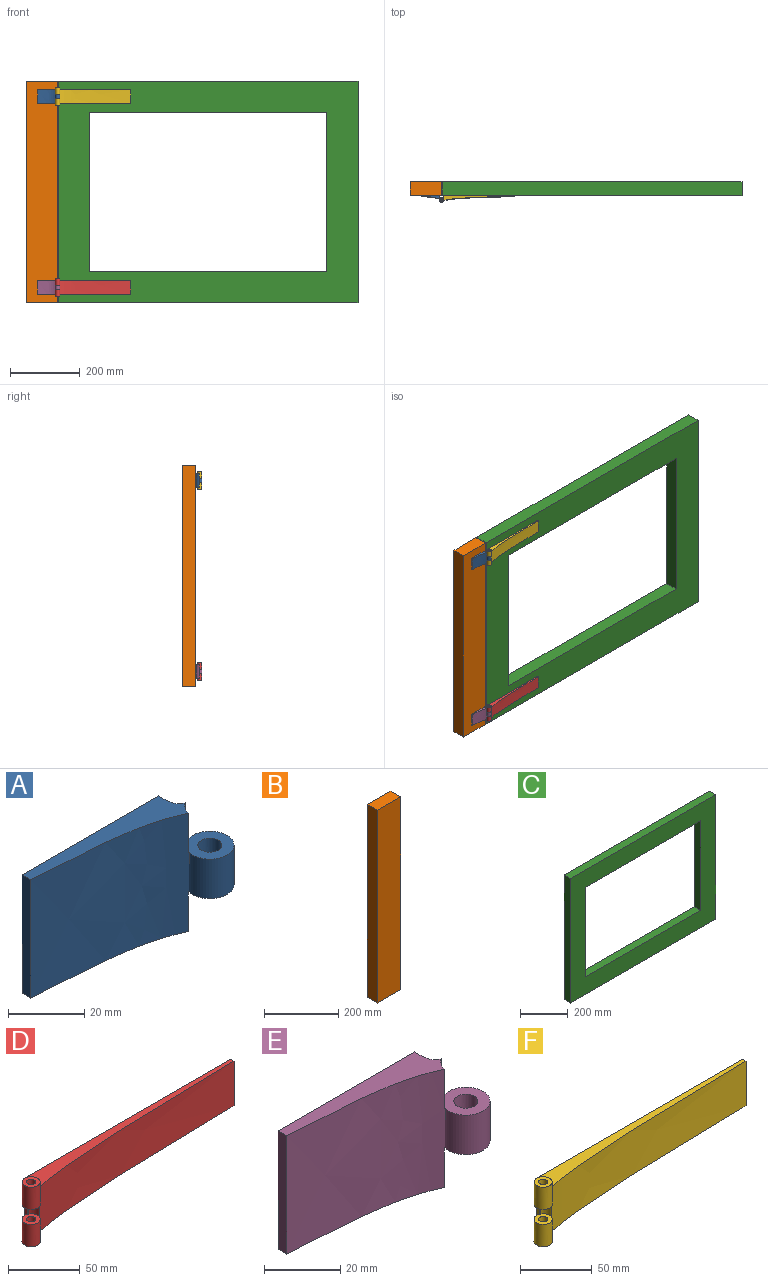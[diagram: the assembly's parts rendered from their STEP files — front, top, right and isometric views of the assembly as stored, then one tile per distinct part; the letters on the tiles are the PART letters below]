
ASSEMBLY  parts=6 mates=5
PART A: 13 faces, bbox 63.5x19.1x38.1 mm
  f0: cylinder r=6.35mm len=12.7mm, axis (0,0,1), area 443.4mm2, adj f1,f5,f8,f10
  f1: extruded ~38.1x4.05mm, area 204.5mm2, adj f0,f2,f6,f7,f8,f9,f10,f11
  f2: plane 38.1x3.18mm, normal (1,0,0), area 121mm2, adj f1,f3,f6,f7
  f3: plane 50.8x38.1mm, normal (0,1,0), area 1935.5mm2, adj f2,f4,f6,f7
  f4: plane 38.1x3.18mm, normal (-1,0,0), area 121mm2, adj f3,f5,f6,f7
  f5: extruded ~51x38.1mm, area 1971.3mm2, adj f0,f4,f6,f7,f8,f9,f10,f11
  f6: plane 53.65x11.1mm, normal (0,0,-1), area 293.4mm2, adj f1,f2,f3,f4,f5,f11
  f7: plane 53.65x11.1mm, normal (0,0,1), area 293.4mm2, adj f1,f2,f3,f4,f5,f9
  f8: plane 12.73x12.7mm, normal (0,0,1), area 96.3mm2, adj f0,f1,f5,f9,f12
  f9: cylinder r=6.6mm len=12.7mm, axis (0,0,1), area 62.1mm2, adj f1,f5,f7,f8
  f10: plane 12.73x12.7mm, normal (0,0,-1), area 96.3mm2, adj f0,f1,f5,f11,f12
  f11: cylinder r=6.6mm len=12.7mm, axis (0,0,-1), area 62.1mm2, adj f1,f5,f6,f10
  f12: cylinder r=3.17mm len=12.7mm, axis (0,0,1), area 253.4mm2, adj f8,f10
PART B: 6 faces, bbox 88.9x38.1x635 mm
  f0: plane 88.9x38.1mm, normal (0,0,1), area 3387.1mm2, adj f1,f3,f4,f5
  f1: plane 635x38.1mm, normal (-1,0,0), area 24193.5mm2, adj f0,f2,f4,f5
  f2: plane 88.9x38.1mm, normal (0,0,-1), area 3387.1mm2, adj f1,f3,f4,f5
  f3: plane 635x38.1mm, normal (1,0,0), area 24193.5mm2, adj f0,f2,f4,f5
  f4: plane 635x88.9mm, normal (0,-1,0), area 56451.5mm2, adj f0,f1,f2,f3
  f5: plane 635x88.9mm, normal (0,1,0), area 56451.5mm2, adj f0,f1,f2,f3
PART C: 10 faces, bbox 857.3x38.1x635 mm
  f0: plane 857.25x38.1mm, normal (0,0,1), area 32661.2mm2, adj f1,f7,f8,f9
  f1: plane 635x38.1mm, normal (-1,0,0), area 24193.5mm2, adj f0,f2,f8,f9
  f2: plane 857.25x38.1mm, normal (0,0,-1), area 32661.2mm2, adj f1,f7,f8,f9
  f3: plane 457.2x38.1mm, normal (1,0,0), area 17419.3mm2, adj f4,f6,f8,f9
  f4: plane 679.45x38.1mm, normal (0,0,-1), area 25887mm2, adj f3,f5,f8,f9
  f5: plane 457.2x38.1mm, normal (-1,0,0), area 17419.3mm2, adj f4,f6,f8,f9
  f6: plane 679.45x38.1mm, normal (0,0,1), area 25887mm2, adj f3,f5,f8,f9
  f7: plane 635x38.1mm, normal (1,0,0), area 24193.5mm2, adj f0,f2,f8,f9
  f8: plane 857.25x635mm, normal (0,-1,0), area 233709.2mm2, adj f0,f1,f2,f3,f4,f5,f6,f7
  f9: plane 857.25x635mm, normal (0,1,0), area 233709.2mm2, adj f0,f1,f2,f3,f4,f5,f6,f7
PART D: 16 faces, bbox 215.9x19.1x50.8 mm
  f0: extruded ~38.1x4.01mm, area 210.1mm2, adj f1,f4,f6,f9,f10,f11,f12,f13
  f1: cylinder r=6.35mm len=19.05mm, axis (0,0,1), area 646.3mm2, adj f0,f2,f5,f9,f12
  f2: extruded ~203.6x38.1mm, area 7775.7mm2, adj f1,f6,f7,f9,f10,f11,f12,f13
  f3: plane 12.7x12.7mm, normal (0,0,1), area 95mm2, adj f6,f14
  f4: plane 38.1x3.18mm, normal (-1,0,0), area 121mm2, adj f0,f8,f9,f10
  f5: plane 12.7x12.7mm, normal (0,0,-1), area 95mm2, adj f1,f15
  f6: cylinder r=6.35mm len=19.05mm, axis (0,0,1), area 646.3mm2, adj f0,f2,f3,f10,f13
  f7: plane 38.1x3.18mm, normal (1,0,0), area 121mm2, adj f2,f8,f9,f10
  f8: plane 203.2x38.1mm, normal (0,1,0), area 7741.9mm2, adj f4,f7,f9,f10
  f9: plane 206.4x14.93mm, normal (0,0,-1), area 1343.8mm2, adj f0,f1,f2,f4,f7,f8
  f10: plane 206.4x14.93mm, normal (0,0,1), area 1343.8mm2, adj f0,f2,f4,f6,f7,f8
  f11: cylinder r=6.6mm len=12.7mm, axis (0,0,1), area 113.2mm2, adj f0,f2,f12,f13
  f12: plane 12.95x12.7mm, normal (0,0,1), area 97.3mm2, adj f0,f1,f2,f11,f15
  f13: plane 12.95x12.7mm, normal (0,0,-1), area 97.3mm2, adj f0,f2,f6,f11,f14
  f14: cylinder r=3.17mm len=19.05mm, axis (0,0,1), area 380mm2, adj f3,f13
  f15: cylinder r=3.17mm len=19.05mm, axis (0,0,1), area 380mm2, adj f5,f12
PART E: 13 faces, bbox 63.5x19.1x38.1 mm
  f0: cylinder r=6.35mm len=12.7mm, axis (0,0,1), area 443.4mm2, adj f1,f5,f8,f10
  f1: extruded ~38.1x4.05mm, area 204.5mm2, adj f0,f2,f6,f7,f8,f9,f10,f11
  f2: plane 38.1x3.18mm, normal (1,0,0), area 121mm2, adj f1,f3,f6,f7
  f3: plane 50.8x38.1mm, normal (0,1,0), area 1935.5mm2, adj f2,f4,f6,f7
  f4: plane 38.1x3.18mm, normal (-1,0,0), area 121mm2, adj f3,f5,f6,f7
  f5: extruded ~51x38.1mm, area 1971.3mm2, adj f0,f4,f6,f7,f8,f9,f10,f11
  f6: plane 53.65x11.1mm, normal (0,0,-1), area 293.4mm2, adj f1,f2,f3,f4,f5,f11
  f7: plane 53.65x11.1mm, normal (0,0,1), area 293.4mm2, adj f1,f2,f3,f4,f5,f9
  f8: plane 12.73x12.7mm, normal (0,0,1), area 96.3mm2, adj f0,f1,f5,f9,f12
  f9: cylinder r=6.6mm len=12.7mm, axis (0,0,1), area 62.1mm2, adj f1,f5,f7,f8
  f10: plane 12.73x12.7mm, normal (0,0,-1), area 96.3mm2, adj f0,f1,f5,f11,f12
  f11: cylinder r=6.6mm len=12.7mm, axis (0,0,-1), area 62.1mm2, adj f1,f5,f6,f10
  f12: cylinder r=3.17mm len=12.7mm, axis (0,0,1), area 253.4mm2, adj f8,f10
PART F: 16 faces, bbox 215.9x19.1x50.8 mm
  f0: extruded ~38.1x4.01mm, area 210.1mm2, adj f1,f4,f6,f9,f10,f11,f12,f13
  f1: cylinder r=6.35mm len=19.05mm, axis (0,0,1), area 646.3mm2, adj f0,f2,f5,f9,f12
  f2: extruded ~203.6x38.1mm, area 7775.7mm2, adj f1,f6,f7,f9,f10,f11,f12,f13
  f3: plane 12.7x12.7mm, normal (0,0,1), area 95mm2, adj f6,f14
  f4: plane 38.1x3.18mm, normal (-1,0,0), area 121mm2, adj f0,f8,f9,f10
  f5: plane 12.7x12.7mm, normal (0,0,-1), area 95mm2, adj f1,f15
  f6: cylinder r=6.35mm len=19.05mm, axis (0,0,1), area 646.3mm2, adj f0,f2,f3,f10,f13
  f7: plane 38.1x3.18mm, normal (1,0,0), area 121mm2, adj f2,f8,f9,f10
  f8: plane 203.2x38.1mm, normal (0,1,0), area 7741.9mm2, adj f4,f7,f9,f10
  f9: plane 206.4x14.93mm, normal (0,0,-1), area 1343.8mm2, adj f0,f1,f2,f4,f7,f8
  f10: plane 206.4x14.93mm, normal (0,0,1), area 1343.8mm2, adj f0,f2,f4,f6,f7,f8
  f11: cylinder r=6.6mm len=12.7mm, axis (0,0,1), area 113.2mm2, adj f0,f2,f12,f13
  f12: plane 12.95x12.7mm, normal (0,0,1), area 97.3mm2, adj f0,f1,f2,f11,f15
  f13: plane 12.95x12.7mm, normal (0,0,-1), area 97.3mm2, adj f0,f2,f6,f11,f14
  f14: cylinder r=3.17mm len=19.05mm, axis (0,0,1), area 380mm2, adj f3,f13
  f15: cylinder r=3.17mm len=19.05mm, axis (0,0,1), area 380mm2, adj f5,f12
PLACE A at identity
PLACE B at identity fixed
PLACE C rot(axis=(0,0,-1),0deg) t=(332.72,0,-22.44)mm
PLACE D rot(axis=(0,0,-1),0deg) t=(332.39,0,-22.44)mm
PLACE E at identity
PLACE F rot(axis=(0,0,1),0deg) t=(332.39,0,-22.44)mm
MATE fastened C.f8 <-> F.f8  axis (0,-1,0) through (332.39,-38.1,4.96)mm
MATE revolute A.f0 <-> F.f1  axis (0,0,1) through (-98.16,-50.8,284.36)mm
MATE fastened B.f4 <-> E.f3  axis (0,-1,0) through (-144.2,-38.1,4.96)mm
MATE fastened C.f8 <-> D.f8  axis (0,-1,0) through (332.39,-38.1,4.96)mm
MATE fastened B.f4 <-> A.f3  axis (0,-1,0) through (-144.2,-38.1,4.96)mm
